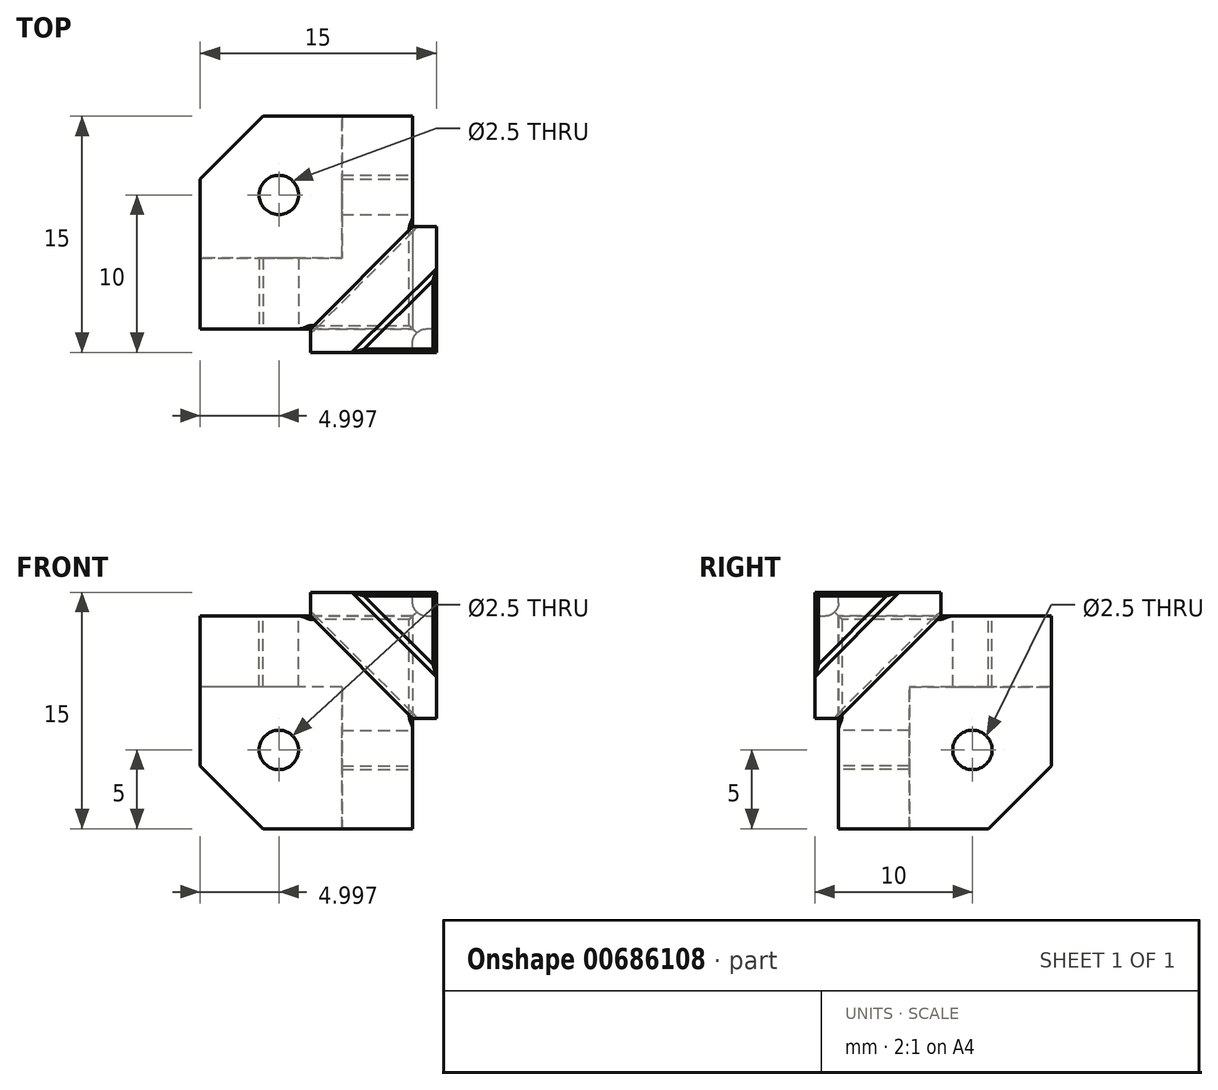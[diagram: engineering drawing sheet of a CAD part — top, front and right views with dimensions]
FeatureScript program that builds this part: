
annotation { "Feature Type Name" : "Feature", "Feature Type Description" : "" }
export const myFeature = defineFeature(function(context is Context, id is Id, definition is map)
    precondition{}
    {
        {
            var Q0;
            Q0=qCreatedBy(makeId("Front.planeOp"),FACE);
            var sketch = newSketch(context, id + "F0", { "sketchPlane" : qUnion([Q0])});
            skLineSegment(sketch, "E0", {"start": v(7.23, 37.22) * mm, "end": v(15.23, 37.22) * mm});
            skLineSegment(sketch, "E1", {"start": v(15.23, 37.22) * mm, "end": v(15.23, 29.22) * mm});
            skLineSegment(sketch, "E2", {"start": v(15.23, 29.22) * mm, "end": v(13.73, 29.22) * mm});
            skLineSegment(sketch, "E3", {"start": v(13.73, 29.22) * mm, "end": v(7.23, 35.72) * mm});
            skLineSegment(sketch, "E4", {"start": v(7.23, 35.72) * mm, "end": v(7.23, 37.22) * mm});
            skLineSegment(sketch, "E5", {"start": v(15.23, 29.22) * mm, "end": v(15.23, 27.22) * mm, "construction": true});
            skLineSegment(sketch, "E6", {"start": v(15.23, 27.22) * mm, "end": v(5.23, 27.22) * mm, "construction": true});
            skCircle(sketch, "E7", {"center": v(5.23, 27.22) * mm, "radius": 1.25 * mm});
            skLineSegment(sketch, "E8", {"start": v(7.23, 37.22) * mm, "end": v(0.23, 37.22) * mm});
            skLineSegment(sketch, "E9", {"start": v(0.23, 37.22) * mm, "end": v(0.23, 26.22) * mm});
            skLineSegment(sketch, "E10", {"start": v(0.23, 26.22) * mm, "end": v(4.23, 22.22) * mm});
            skLineSegment(sketch, "E11", {"start": v(4.23, 22.22) * mm, "end": v(15.23, 22.22) * mm});
            skLineSegment(sketch, "E12", {"start": v(15.23, 22.22) * mm, "end": v(15.23, 29.22) * mm});
            skSolve(sketch);
        }
        {
            var Q0;
            Q0=makeQuery(id+"F0.imprint","IMPRINT",FACE,{"disambiguationData":[TD([[makeQuery(id+"F0.imprint","IMPRINT",EDGE,{"derivedFrom":sQuery(id+"F0.wireOp",EDGE,"E0")}),-1.0]])]});
            extrude(context, id + "F1", {"entities" : qUnion([Q0]), "depth" : 1.5 * mm, "offsetDistance" : 25 * mm});
        }
        {
            var Q0;
            Q0=makeQuery(id+"F0.imprint","IMPRINT",FACE,{"disambiguationData":[TD([[makeQuery(id+"F0.imprint","IMPRINT",EDGE,{"derivedFrom":sQuery(id+"F0.wireOp",EDGE,"E2")}),1.0]])]});
            var Q1;
            Q1=makeQuery(id+"F0.imprint","IMPRINT",FACE,{"disambiguationData":[TD([[makeQuery(id+"F0.imprint","IMPRINT",EDGE,{"derivedFrom":sQuery(id+"F0.wireOp",EDGE,"E0")}),-1.0]])]});
            extrude(context, id + "F2", {"entities" : qUnion([Q0, Q1]), "operationType" : NewBodyOperationType.ADD, "oppositeDirection" : true, "depth" : 3.5 * mm, "offsetDistance" : 25 * mm});
        }
        {
            var Q0;
            {var subQ0=sQuery(id+"F0.wireOp",EDGE,"E0");Q0=makeQuery(id+"F2.boolean.opBoolean","MERGE",FACE,{"derivedFrom":[makeQuery(id+"F1.opExtrude","SWEPT_FACE",FACE,{"disambiguationData":[OSD([subQ0])]}),makeQuery(id+"F2.opExtrude","SWEPT_FACE",FACE,{"disambiguationData":[OSD([subQ0,sQuery(id+"F0.wireOp",EDGE,"E8")])]})]});}
            var sketch = newSketch(context, id + "F3", { "sketchPlane" : qUnion([Q0])});
            skLineSegment(sketch, "E13", {"start": v(7.23, -1.5) * mm, "end": v(15.23, -1.5) * mm});
            skLineSegment(sketch, "E14", {"start": v(15.23, -1.5) * mm, "end": v(15.23, 6.5) * mm});
            skLineSegment(sketch, "E15", {"start": v(15.23, 6.5) * mm, "end": v(13.73, 6.5) * mm});
            skLineSegment(sketch, "E16", {"start": v(13.73, 6.5) * mm, "end": v(7.23, 0) * mm});
            skLineSegment(sketch, "E17", {"start": v(13.73, 6.5) * mm, "end": v(13.73, 13.5) * mm});
            skLineSegment(sketch, "E18", {"start": v(13.73, 13.5) * mm, "end": v(4.23, 13.5) * mm});
            skLineSegment(sketch, "E19", {"start": v(4.23, 13.5) * mm, "end": v(0.23, 9.5) * mm});
            skPoint(sketch, "E19.endSnap0", {"position": v(0.23, 1.75) * mm});
            skLineSegment(sketch, "E20", {"start": v(0.23, 9.5) * mm, "end": v(0.23, 0) * mm});
            skLineSegment(sketch, "E21", {"start": v(8.02, -1.5) * mm, "end": v(5.23, -1.5) * mm, "construction": true});
            skLineSegment(sketch, "E22", {"start": v(5.23, -1.5) * mm, "end": v(5.23, 8.5) * mm, "construction": true});
            skCircle(sketch, "E23", {"center": v(5.23, 8.5) * mm, "radius": 1.25 * mm});
            skSolve(sketch);
        }
        {
            var Q0;
            {var subQ1=sQuery(id+"F3.wireOp",EDGE,"E17");Q0=makeQuery(id+"F3.imprint","IMPRINT",FACE,{"disambiguationData":[TD([[makeQuery(id+"F3.imprint","IMPRINT",EDGE,{"derivedFrom":subQ1}),1.0]])]});}
            var Q1;
            {var subQ3=sQuery(id+"F3.wireOp",EDGE,"E15");Q1=makeQuery(id+"F3.imprint","IMPRINT",FACE,{"disambiguationData":[TD([[makeQuery(id+"F3.imprint","IMPRINT",EDGE,{"derivedFrom":subQ3}),1.0]])]});}
            extrude(context, id + "F4", {"entities" : qUnion([Q0, Q1]), "operationType" : NewBodyOperationType.ADD, "oppositeDirection" : true, "depth" : 5 * mm, "offsetDistance" : 25 * mm});
        }
        {
            var Q0;
            {var subQ1=sQuery(id+"F3.wireOp",EDGE,"E17");Q0=makeQuery(id+"F3.imprint","IMPRINT",FACE,{"disambiguationData":[TD([[makeQuery(id+"F3.imprint","IMPRINT",EDGE,{"derivedFrom":subQ1}),1.0]])]});}
            var Q1;
            {var subQ1=sQuery(id+"F0.wireOp",EDGE,"E8");var subQ2=sQuery(id+"F0.wireOp",EDGE,"E0");var subQ3=makeQuery(id+"F2.opExtrude","CAP_EDGE",EDGE,{"disambiguationData":[OSD([subQ2,subQ1])],"isStart":true});Q1=makeQuery(id+"F3.imprint","IMPRINT",FACE,{"disambiguationData":[TD([[makeQuery(id+"F3.imprint","IMPRINT",EDGE,{"derivedFrom":subQ3}),-1.0]])]});}
            extrude(context, id + "F5", {"entities" : qUnion([Q0, Q1]), "operationType" : NewBodyOperationType.REMOVE, "oppositeDirection" : true, "depth" : 1.5 * mm, "offsetDistance" : 25 * mm});
        }
        {
            var Q0;
            {var subQ0=sQuery(id+"F0.wireOp",EDGE,"E1");Q0=makeQuery(id+"F2.boolean.opBoolean","MERGE",FACE,{"derivedFrom":[makeQuery(id+"F1.opExtrude","SWEPT_FACE",FACE,{"disambiguationData":[OSD([subQ0])]}),makeQuery(id+"F2.opExtrude","SWEPT_FACE",FACE,{"disambiguationData":[OSD([subQ0,sQuery(id+"F0.wireOp",EDGE,"E12")])]})]});}
            var sketch = newSketch(context, id + "F6", { "sketchPlane" : qUnion([Q0])});
            skLineSegment(sketch, "E24", {"start": v(0, 29.22) * mm, "end": v(0, 22.22) * mm});
            skLineSegment(sketch, "E25", {"start": v(0, 22.22) * mm, "end": v(9.5, 22.22) * mm});
            skLineSegment(sketch, "E26", {"start": v(13.5, 35.72) * mm, "end": v(13.5, 26.22) * mm});
            skLineSegment(sketch, "E27", {"start": v(13.5, 26.22) * mm, "end": v(9.5, 22.22) * mm});
            skLineSegment(sketch, "E28", {"start": v(-1.5, 29.22) * mm, "end": v(-1.5, 27.22) * mm, "construction": true});
            skLineSegment(sketch, "E29", {"start": v(-1.5, 27.22) * mm, "end": v(8.5, 27.22) * mm, "construction": true});
            skCircle(sketch, "E30", {"center": v(8.5, 27.22) * mm, "radius": 1.25 * mm});
            skLineSegment(sketch, "E31", {"start": v(13.5, 35.72) * mm, "end": v(6.5, 35.72) * mm});
            skLineSegment(sketch, "E32", {"start": v(6.5, 35.72) * mm, "end": v(0, 29.22) * mm});
            skSolve(sketch);
        }
        {
            var Q0;
            Q0=qSketchRegion(id+"F6",true);
            extrude(context, id + "F7", {"entities" : qUnion([Q0]), "operationType" : NewBodyOperationType.ADD, "oppositeDirection" : true, "depth" : 5 * mm, "offsetDistance" : 25 * mm});
        }
        {
            var Q0;
            {var subQ2=sQuery(id+"F6.wireOp",EDGE,"E24");Q0=makeQuery(id+"F6.imprint","IMPRINT",FACE,{"disambiguationData":[TD([[makeQuery(id+"F6.imprint","IMPRINT",EDGE,{"derivedFrom":subQ2}),-1.0]])]});}
            var Q1;
            Q1=makeQuery(id+"F6.imprint","IMPRINT",FACE,{"disambiguationData":[TD([[makeQuery(id+"F6.imprint","IMPRINT",EDGE,{"derivedFrom":sQuery(id+"F6.wireOp",EDGE,"E26")}),-1.0]])]});
            var Q2;
            {var subQ1=sQuery(id+"F3.wireOp",EDGE,"E14");var subQ2=makeQuery(id+"F4.opExtrude","CAP_EDGE",EDGE,{"disambiguationData":[OSD([subQ1])],"isStart":false});Q2=makeQuery(id+"F6.imprint","IMPRINT",FACE,{"disambiguationData":[TD([[makeQuery(id+"F6.imprint","IMPRINT",EDGE,{"derivedFrom":subQ2}),1.0]])]});}
            extrude(context, id + "F8", {"entities" : qUnion([Q0, Q1, Q2]), "operationType" : NewBodyOperationType.REMOVE, "oppositeDirection" : true, "depth" : 1.5 * mm, "offsetDistance" : 25 * mm});
        }
        {
            var Q0;
            Q0=makeQuery(id+"F1.opExtrude","CAP_FACE",FACE,{"disambiguationData":[OSD([sQuery(id+"F0.wireOp",EDGE,"E0"),sQuery(id+"F0.wireOp",EDGE,"E1"),sQuery(id+"F0.wireOp",EDGE,"E2"),sQuery(id+"F0.wireOp",EDGE,"E3"),sQuery(id+"F0.wireOp",EDGE,"E4")])],"isStart":false});
            var sketch = newSketch(context, id + "F9", { "sketchPlane" : qUnion([Q0])});
            skLineSegment(sketch, "E33", {"start": v(15.23, 37.22) * mm, "end": v(15.23, 32.22) * mm});
            skLineSegment(sketch, "E34", {"start": v(15.23, 32.22) * mm, "end": v(10.23, 37.22) * mm});
            skLineSegment(sketch, "E35", {"start": v(10.23, 37.22) * mm, "end": v(15.23, 37.22) * mm});
            skSolve(sketch);
        }
        {
            var Q0;
            Q0=makeQuery(id+"F9.imprint","IMPRINT",FACE,{"disambiguationData":[TD([[makeQuery(id+"F9.imprint","IMPRINT",EDGE,{"derivedFrom":sQuery(id+"F9.wireOp",EDGE,"E33")}),-1.0]])]});
            extrude(context, id + "F10", {"entities" : qUnion([Q0]), "operationType" : NewBodyOperationType.REMOVE, "oppositeDirection" : true, "depth" : 5 * mm, "offsetDistance" : 25 * mm});
        }
        {
            var Q0;
            Q0=makeQuery(id+"F10.boolean.opBoolean","COPY",EDGE,{"derivedFrom":makeQuery(id+"F10.opExtrude","CAP_EDGE",EDGE,{"disambiguationData":[OSD([sQuery(id+"F9.wireOp",EDGE,"E34")])],"isStart":false})});
            chamfer(context, id + "F11", {"entities" : qUnion([Q0]), "chamferType" : ChamferType.OFFSET_ANGLE, "width" : 5 * mm, "oppositeDirection" : false, "angle" : 35.4 * degree, "tangentPropagation" : true});
        }
        {
            var Q0;
            Q0=makeQuery(id+"F11.opChamfer","BLEND_EDGE",EDGE,{"blendedFrom":[makeQuery(id+"F10.boolean.opBoolean","COPY",EDGE,{"derivedFrom":makeQuery(id+"F10.opExtrude","CAP_EDGE",EDGE,{"disambiguationData":[OSD([sQuery(id+"F9.wireOp",EDGE,"E34")])],"isStart":false})}),makeQuery(id+"F1.opExtrude","CAP_FACE",FACE,{"disambiguationData":[OSD([sQuery(id+"F0.wireOp",EDGE,"E0"),sQuery(id+"F0.wireOp",EDGE,"E1"),sQuery(id+"F0.wireOp",EDGE,"E2"),sQuery(id+"F0.wireOp",EDGE,"E3"),sQuery(id+"F0.wireOp",EDGE,"E4")])],"isStart":false})],"blendedInto":[makeQuery(id+"F1.opExtrude","CAP_FACE",FACE,{"disambiguationData":[OSD([sQuery(id+"F0.wireOp",EDGE,"E0"),sQuery(id+"F0.wireOp",EDGE,"E1"),sQuery(id+"F0.wireOp",EDGE,"E2"),sQuery(id+"F0.wireOp",EDGE,"E3"),sQuery(id+"F0.wireOp",EDGE,"E4")])],"isStart":false})]});
            var Q1;
            {var subQ0=sQuery(id+"F0.wireOp",EDGE,"E8");var subQ1=sQuery(id+"F0.wireOp",EDGE,"E0");Q1=makeQuery(id+"F11.opChamfer","BLEND_EDGE",EDGE,{"blendedFrom":[makeQuery(id+"F10.boolean.opBoolean","COPY",EDGE,{"derivedFrom":makeQuery(id+"F10.opExtrude","CAP_EDGE",EDGE,{"disambiguationData":[OSD([sQuery(id+"F9.wireOp",EDGE,"E34")])],"isStart":false})}),makeQuery(id+"F4.boolean.opBoolean","MERGE",FACE,{"derivedFrom":[makeQuery(id+"F2.boolean.opBoolean","MERGE",FACE,{"derivedFrom":[makeQuery(id+"F1.opExtrude","SWEPT_FACE",FACE,{"disambiguationData":[OSD([subQ1])]}),makeQuery(id+"F2.opExtrude","SWEPT_FACE",FACE,{"disambiguationData":[OSD([subQ1,subQ0])]})]}),makeQuery(id+"F4.opExtrude","CAP_FACE",FACE,{"disambiguationData":[OSD([subQ1,subQ0,sQuery(id+"F3.wireOp",EDGE,"id0TNCpU-tjdV-AgSU-QIlH-1rNdUmwGPP8J"),sQuery(id+"F3.wireOp",EDGE,"mGFVvrbr-tIrU-syV4-yza1-VgwdehKtnJvE"),sQuery(id+"F3.wireOp",EDGE,"wSTTxPhp-j6Tf-tGPT-JtDE-c5HYP9l80gTy"),sQuery(id+"F3.wireOp",EDGE,"6f74HBZF-W9bh-Bztp-LMnC-ap8Q1K5RPxhI"),sQuery(id+"F3.wireOp",EDGE,"pXlPqK1o-hzZR-9fDG-u2KL-nj3FlQz3lFwb")])],"isStart":true})]})],"blendedInto":[makeQuery(id+"F4.boolean.opBoolean","MERGE",FACE,{"derivedFrom":[makeQuery(id+"F2.boolean.opBoolean","MERGE",FACE,{"derivedFrom":[makeQuery(id+"F1.opExtrude","SWEPT_FACE",FACE,{"disambiguationData":[OSD([subQ1])]}),makeQuery(id+"F2.opExtrude","SWEPT_FACE",FACE,{"disambiguationData":[OSD([subQ1,subQ0])]})]}),makeQuery(id+"F4.opExtrude","CAP_FACE",FACE,{"disambiguationData":[OSD([subQ1,subQ0,sQuery(id+"F3.wireOp",EDGE,"id0TNCpU-tjdV-AgSU-QIlH-1rNdUmwGPP8J"),sQuery(id+"F3.wireOp",EDGE,"mGFVvrbr-tIrU-syV4-yza1-VgwdehKtnJvE"),sQuery(id+"F3.wireOp",EDGE,"wSTTxPhp-j6Tf-tGPT-JtDE-c5HYP9l80gTy"),sQuery(id+"F3.wireOp",EDGE,"6f74HBZF-W9bh-Bztp-LMnC-ap8Q1K5RPxhI"),sQuery(id+"F3.wireOp",EDGE,"pXlPqK1o-hzZR-9fDG-u2KL-nj3FlQz3lFwb")])],"isStart":true})]})]});}
            var Q2;
            {var subQ0=sQuery(id+"F0.wireOp",EDGE,"E1");Q2=makeQuery(id+"F11.opChamfer","BLEND_EDGE",EDGE,{"blendedFrom":[makeQuery(id+"F10.boolean.opBoolean","COPY",EDGE,{"derivedFrom":makeQuery(id+"F10.opExtrude","CAP_EDGE",EDGE,{"disambiguationData":[OSD([sQuery(id+"F9.wireOp",EDGE,"E34")])],"isStart":false})}),makeQuery(id+"F7.boolean.opBoolean","MERGE",FACE,{"derivedFrom":[makeQuery(id+"F2.boolean.opBoolean","MERGE",FACE,{"derivedFrom":[makeQuery(id+"F1.opExtrude","SWEPT_FACE",FACE,{"disambiguationData":[OSD([subQ0])]}),makeQuery(id+"F2.opExtrude","SWEPT_FACE",FACE,{"disambiguationData":[OSD([subQ0,sQuery(id+"F0.wireOp",EDGE,"E12")])]})]}),makeQuery(id+"F7.opExtrude","CAP_FACE",FACE,{"disambiguationData":[OSD([sQuery(id+"F6.wireOp",EDGE,"bjqw6rF1-9aoZ-1MRt-8oHp-ZjFiTM0oOFLL"),sQuery(id+"F6.wireOp",EDGE,"E24"),sQuery(id+"F6.wireOp",EDGE,"E25"),sQuery(id+"F6.wireOp",EDGE,"4vnc1qx3-YKp5-J8BV-yxKJ-AHBmvpOXDA1h"),sQuery(id+"F6.wireOp",EDGE,"E26"),sQuery(id+"F6.wireOp",EDGE,"E27"),sQuery(id+"F6.wireOp",EDGE,"E30")])],"isStart":true})]})],"blendedInto":[makeQuery(id+"F7.boolean.opBoolean","MERGE",FACE,{"derivedFrom":[makeQuery(id+"F2.boolean.opBoolean","MERGE",FACE,{"derivedFrom":[makeQuery(id+"F1.opExtrude","SWEPT_FACE",FACE,{"disambiguationData":[OSD([subQ0])]}),makeQuery(id+"F2.opExtrude","SWEPT_FACE",FACE,{"disambiguationData":[OSD([subQ0,sQuery(id+"F0.wireOp",EDGE,"E12")])]})]}),makeQuery(id+"F7.opExtrude","CAP_FACE",FACE,{"disambiguationData":[OSD([sQuery(id+"F6.wireOp",EDGE,"bjqw6rF1-9aoZ-1MRt-8oHp-ZjFiTM0oOFLL"),sQuery(id+"F6.wireOp",EDGE,"E24"),sQuery(id+"F6.wireOp",EDGE,"E25"),sQuery(id+"F6.wireOp",EDGE,"4vnc1qx3-YKp5-J8BV-yxKJ-AHBmvpOXDA1h"),sQuery(id+"F6.wireOp",EDGE,"E26"),sQuery(id+"F6.wireOp",EDGE,"E27"),sQuery(id+"F6.wireOp",EDGE,"E30")])],"isStart":true})]})]});}
            chamfer(context, id + "F12", {"entities" : qUnion([Q0, Q1, Q2]), "width" : .5 * mm, "tangentPropagation" : true});
        }
        {
            var Q0;
            {var subQ0=sQuery(id+"F0.wireOp",EDGE,"E2");Q0=makeQuery(id+"F8.boolean.opBoolean","MERGE",VERTEX,{"derivedFrom":[makeQuery(id+"F1.opExtrude","CAP_VERTEX",VERTEX,{"disambiguationData":[OSD([subQ0,sQuery(id+"F0.wireOp",EDGE,"E3")])],"isStart":true}),makeQuery(id+"F8.opExtrude","CAP_VERTEX",VERTEX,{"disambiguationData":[OSD([sQuery(id+"F0.wireOp",EDGE,"E1"),subQ0,sQuery(id+"F0.wireOp",EDGE,"E12"),sQuery(id+"F6.wireOp",EDGE,"E24"),sQuery(id+"F6.wireOp",EDGE,"E32")])],"isStart":false})]});}
            var Q1;
            {var subQ0=sQuery(id+"F0.wireOp",EDGE,"E4");Q1=makeQuery(id+"F5.boolean.opBoolean","MERGE",VERTEX,{"derivedFrom":[makeQuery(id+"F1.opExtrude","CAP_VERTEX",VERTEX,{"disambiguationData":[OSD([sQuery(id+"F0.wireOp",EDGE,"E3"),subQ0])],"isStart":true}),makeQuery(id+"F5.opExtrude","CAP_VERTEX",VERTEX,{"disambiguationData":[OSD([sQuery(id+"F0.wireOp",EDGE,"E0"),subQ0,sQuery(id+"F0.wireOp",EDGE,"E8"),sQuery(id+"F3.wireOp",EDGE,"E16")])],"isStart":false})]});}
            var Q2;
            {var subQ0=sQuery(id+"F3.wireOp",EDGE,"E15");Q2=makeQuery(id+"F8.boolean.opBoolean","MERGE",VERTEX,{"derivedFrom":[makeQuery(id+"F5.boolean.opBoolean","COPY",VERTEX,{"derivedFrom":makeQuery(id+"F5.opExtrude","CAP_VERTEX",VERTEX,{"disambiguationData":[OSD([subQ0,sQuery(id+"F3.wireOp",EDGE,"E16"),sQuery(id+"F3.wireOp",EDGE,"E17")])],"isStart":false})}),makeQuery(id+"F8.opExtrude","CAP_VERTEX",VERTEX,{"disambiguationData":[OSD([sQuery(id+"F3.wireOp",EDGE,"E14"),subQ0,sQuery(id+"F6.wireOp",EDGE,"E31"),sQuery(id+"F6.wireOp",EDGE,"E32")])],"isStart":false})]});}
            cPlane(context, id + "F13", {"entities" : qUnion([Q0, Q1, Q2]), "cplaneType" : CPlaneType.THREE_POINT, "offset" : 25 * mm, "width" : 150 * mm, "height" : 150 * mm});
        }
        {
            var Q0;
            Q0=qCreatedBy(id+"F13.planeOp",FACE);
            var sketch = newSketch(context, id + "F14", { "sketchPlane" : qUnion([Q0])});
            skLineSegment(sketch, "E36", {"start": v(-8.68, 25.26) * mm, "end": v(-0.72, 20.66) * mm});
            skLineSegment(sketch, "E37", {"start": v(-0.72, 29.85) * mm, "end": v(-8.68, 25.26) * mm});
            skLineSegment(sketch, "E38", {"start": v(-0.72, 20.66) * mm, "end": v(-0.72, 29.85) * mm});
            skLineSegment(sketch, "E39.0", {"start": v(-0.92, 29.5) * mm, "end": v(-8.28, 25.26) * mm});
            skLineSegment(sketch, "E39.1", {"start": v(-0.92, 21) * mm, "end": v(-0.92, 29.5) * mm});
            skLineSegment(sketch, "E39.2", {"start": v(-8.28, 25.26) * mm, "end": v(-0.92, 21) * mm});
            skLineSegment(sketch, "E40.0", {"start": v(0.16, 31.38) * mm, "end": v(-10.44, 25.26) * mm});
            skLineSegment(sketch, "E40.1", {"start": v(0.16, 19.14) * mm, "end": v(0.16, 31.38) * mm});
            skLineSegment(sketch, "E40.2", {"start": v(-10.44, 25.26) * mm, "end": v(0.16, 19.14) * mm});
            skSolve(sketch);
        }
        {
            var Q0;
            Q0=qSketchRegion(id+"F14",true);
            var Q1;
            Q1=makeQuery(id+"F14.imprint","IMPRINT",FACE,{"disambiguationData":[TD([[makeQuery(id+"F14.imprint","IMPRINT",EDGE,{"derivedFrom":sQuery(id+"F14.wireOp",EDGE,"E36")}),1.0]])]});
            extrude(context, id + "F15", {"entities" : qUnion([Q0, Q1]), "operationType" : NewBodyOperationType.REMOVE, "endBound" : BoundingType.SYMMETRIC, "depth" : .6 * mm, "offsetDistance" : 25 * mm});
        }
        {
            var Q0;
            Q0=makeQuery(id+"F15.boolean.opBoolean","COPY",EDGE,{"derivedFrom":makeQuery(id+"F15.opExtrude","CAP_EDGE",EDGE,{"disambiguationData":[OSD([sQuery(id+"F14.wireOp",EDGE,"E39.0")])],"isStart":true})});
            var Q1;
            Q1=makeQuery(id+"F15.boolean.opBoolean","COPY",EDGE,{"derivedFrom":makeQuery(id+"F15.opExtrude","CAP_EDGE",EDGE,{"disambiguationData":[OSD([sQuery(id+"F14.wireOp",EDGE,"E39.1")])],"isStart":true})});
            var Q2;
            Q2=makeQuery(id+"F15.boolean.opBoolean","COPY",EDGE,{"derivedFrom":makeQuery(id+"F15.opExtrude","CAP_EDGE",EDGE,{"disambiguationData":[OSD([sQuery(id+"F14.wireOp",EDGE,"E39.0")])],"isStart":false})});
            var Q3;
            Q3=makeQuery(id+"F15.boolean.opBoolean","COPY",EDGE,{"derivedFrom":makeQuery(id+"F15.opExtrude","CAP_EDGE",EDGE,{"disambiguationData":[OSD([sQuery(id+"F14.wireOp",EDGE,"E39.1")])],"isStart":false})});
            var Q4;
            Q4=makeQuery(id+"F15.boolean.opBoolean","COPY",EDGE,{"derivedFrom":makeQuery(id+"F15.opExtrude","CAP_EDGE",EDGE,{"disambiguationData":[OSD([sQuery(id+"F14.wireOp",EDGE,"E39.2")])],"isStart":true})});
            var Q5;
            Q5=makeQuery(id+"F15.boolean.opBoolean","COPY",EDGE,{"derivedFrom":makeQuery(id+"F15.opExtrude","CAP_EDGE",EDGE,{"disambiguationData":[OSD([sQuery(id+"F14.wireOp",EDGE,"E39.2")])],"isStart":false})});
            fillet(context, id + "F16", {"entities" : qUnion([Q0, Q1, Q2, Q3, Q4, Q5]), "radius" : .3 * mm, "tangentPropagation" : true, "allowEdgeOverflow" : false});
        }
        {
            var Q0;
            Q0=makeQuery(id+"F15.boolean.opBoolean","INTERSECT",EDGE,{"derivedFrom":[makeQuery(id+"F8.boolean.opBoolean","COPY",FACE,{"derivedFrom":makeQuery(id+"F8.opExtrude","SWEPT_FACE",FACE,{"disambiguationData":[OSD([sQuery(id+"F6.wireOp",EDGE,"E32")])]})}),makeQuery(id+"F15.opExtrude","CAP_FACE",FACE,{"disambiguationData":[OSD([sQuery(id+"F14.wireOp",EDGE,"E39.0"),sQuery(id+"F14.wireOp",EDGE,"E39.1"),sQuery(id+"F14.wireOp",EDGE,"E39.2"),sQuery(id+"F14.wireOp",EDGE,"E40.0"),sQuery(id+"F14.wireOp",EDGE,"E40.1"),sQuery(id+"F14.wireOp",EDGE,"E40.2")])],"isStart":false})]});
            var Q1;
            Q1=makeQuery(id+"F15.boolean.opBoolean","INTERSECT",EDGE,{"derivedFrom":[makeQuery(id+"F1.opExtrude","SWEPT_FACE",FACE,{"disambiguationData":[OSD([sQuery(id+"F0.wireOp",EDGE,"E3")])]}),makeQuery(id+"F15.opExtrude","CAP_FACE",FACE,{"disambiguationData":[OSD([sQuery(id+"F14.wireOp",EDGE,"E39.0"),sQuery(id+"F14.wireOp",EDGE,"E39.1"),sQuery(id+"F14.wireOp",EDGE,"E39.2"),sQuery(id+"F14.wireOp",EDGE,"E40.0"),sQuery(id+"F14.wireOp",EDGE,"E40.1"),sQuery(id+"F14.wireOp",EDGE,"E40.2")])],"isStart":false})]});
            var Q2;
            Q2=makeQuery(id+"F15.boolean.opBoolean","INTERSECT",EDGE,{"derivedFrom":[makeQuery(id+"F5.boolean.opBoolean","COPY",FACE,{"derivedFrom":makeQuery(id+"F5.opExtrude","SWEPT_FACE",FACE,{"disambiguationData":[OSD([sQuery(id+"F3.wireOp",EDGE,"E16")])]})}),makeQuery(id+"F15.opExtrude","CAP_FACE",FACE,{"disambiguationData":[OSD([sQuery(id+"F14.wireOp",EDGE,"E39.0"),sQuery(id+"F14.wireOp",EDGE,"E39.1"),sQuery(id+"F14.wireOp",EDGE,"E39.2"),sQuery(id+"F14.wireOp",EDGE,"E40.0"),sQuery(id+"F14.wireOp",EDGE,"E40.1"),sQuery(id+"F14.wireOp",EDGE,"E40.2")])],"isStart":false})]});
            fillet(context, id + "F17", {"entities" : qUnion([Q0, Q1, Q2]), "radius" : 1 * mm, "tangentPropagation" : true, "allowEdgeOverflow" : false});
        }
        {
            var Q0;
            Q0=makeQuery(id+"F15.boolean.opBoolean","INTERSECT",EDGE,{"derivedFrom":[makeQuery(id+"F2.opExtrude","CAP_FACE",FACE,{"disambiguationData":[OSD([sQuery(id+"F0.wireOp",EDGE,"E0"),sQuery(id+"F0.wireOp",EDGE,"E1"),sQuery(id+"F0.wireOp",EDGE,"E7"),sQuery(id+"F0.wireOp",EDGE,"E8"),sQuery(id+"F0.wireOp",EDGE,"E9"),sQuery(id+"F0.wireOp",EDGE,"E10"),sQuery(id+"F0.wireOp",EDGE,"E11"),sQuery(id+"F0.wireOp",EDGE,"E12")])],"isStart":true}),makeQuery(id+"F15.opExtrude","CAP_FACE",FACE,{"disambiguationData":[OSD([sQuery(id+"F14.wireOp",EDGE,"E39.0"),sQuery(id+"F14.wireOp",EDGE,"E39.1"),sQuery(id+"F14.wireOp",EDGE,"E39.2"),sQuery(id+"F14.wireOp",EDGE,"E40.0"),sQuery(id+"F14.wireOp",EDGE,"E40.1"),sQuery(id+"F14.wireOp",EDGE,"E40.2")])],"isStart":true})]});
            var Q1;
            Q1=makeQuery(id+"F15.boolean.opBoolean","INTERSECT",EDGE,{"derivedFrom":[makeQuery(id+"F8.boolean.opBoolean","COPY",FACE,{"derivedFrom":makeQuery(id+"F8.opExtrude","CAP_FACE",FACE,{"disambiguationData":[OSD([sQuery(id+"F6.wireOp",EDGE,"E24"),sQuery(id+"F6.wireOp",EDGE,"E25"),sQuery(id+"F6.wireOp",EDGE,"E26"),sQuery(id+"F6.wireOp",EDGE,"E27"),sQuery(id+"F6.wireOp",EDGE,"E30"),sQuery(id+"F6.wireOp",EDGE,"E31"),sQuery(id+"F6.wireOp",EDGE,"E32")])],"isStart":false})}),makeQuery(id+"F15.opExtrude","CAP_FACE",FACE,{"disambiguationData":[OSD([sQuery(id+"F14.wireOp",EDGE,"E39.0"),sQuery(id+"F14.wireOp",EDGE,"E39.1"),sQuery(id+"F14.wireOp",EDGE,"E39.2"),sQuery(id+"F14.wireOp",EDGE,"E40.0"),sQuery(id+"F14.wireOp",EDGE,"E40.1"),sQuery(id+"F14.wireOp",EDGE,"E40.2")])],"isStart":true})]});
            var Q2;
            Q2=makeQuery(id+"F15.boolean.opBoolean","INTERSECT",EDGE,{"derivedFrom":[makeQuery(id+"F7.boolean.opBoolean","MERGE",FACE,{"derivedFrom":[makeQuery(id+"F5.boolean.opBoolean","COPY",FACE,{"derivedFrom":makeQuery(id+"F5.opExtrude","CAP_FACE",FACE,{"disambiguationData":[OSD([sQuery(id+"F0.wireOp",EDGE,"E0"),sQuery(id+"F0.wireOp",EDGE,"E8"),sQuery(id+"F3.wireOp",EDGE,"E16"),sQuery(id+"F3.wireOp",EDGE,"E17"),sQuery(id+"F3.wireOp",EDGE,"E18"),sQuery(id+"F3.wireOp",EDGE,"E19"),sQuery(id+"F3.wireOp",EDGE,"E20"),sQuery(id+"F3.wireOp",EDGE,"E23")])],"isStart":false})}),makeQuery(id+"F7.opExtrude","SWEPT_FACE",FACE,{"disambiguationData":[OSD([sQuery(id+"F6.wireOp",EDGE,"E31")])]})]}),makeQuery(id+"F15.opExtrude","CAP_FACE",FACE,{"disambiguationData":[OSD([sQuery(id+"F14.wireOp",EDGE,"E39.0"),sQuery(id+"F14.wireOp",EDGE,"E39.1"),sQuery(id+"F14.wireOp",EDGE,"E39.2"),sQuery(id+"F14.wireOp",EDGE,"E40.0"),sQuery(id+"F14.wireOp",EDGE,"E40.1"),sQuery(id+"F14.wireOp",EDGE,"E40.2")])],"isStart":true})]});
            fillet(context, id + "F18", {"entities" : qUnion([Q0, Q1, Q2]), "radius" : .2 * mm, "tangentPropagation" : true, "allowEdgeOverflow" : false});
        }
        {
            var Q0;
            Q0=makeQuery(id+"F2.opExtrude","CAP_FACE",FACE,{"disambiguationData":[OSD([sQuery(id+"F0.wireOp",EDGE,"E0"),sQuery(id+"F0.wireOp",EDGE,"E1"),sQuery(id+"F0.wireOp",EDGE,"E7"),sQuery(id+"F0.wireOp",EDGE,"E8"),sQuery(id+"F0.wireOp",EDGE,"E9"),sQuery(id+"F0.wireOp",EDGE,"E10"),sQuery(id+"F0.wireOp",EDGE,"E11"),sQuery(id+"F0.wireOp",EDGE,"E12")])],"isStart":false});
            extrude(context, id + "F19", {"entities" : qUnion([Q0]), "operationType" : NewBodyOperationType.ADD, "depth" : 1 * mm, "offsetDistance" : 25 * mm});
        }
        {
            var Q0;
            Q0=makeQuery(id+"F7.opExtrude","CAP_FACE",FACE,{"disambiguationData":[OSD([sQuery(id+"F6.wireOp",EDGE,"E24"),sQuery(id+"F6.wireOp",EDGE,"E25"),sQuery(id+"F6.wireOp",EDGE,"E26"),sQuery(id+"F6.wireOp",EDGE,"E27"),sQuery(id+"F6.wireOp",EDGE,"E30"),sQuery(id+"F6.wireOp",EDGE,"E31"),sQuery(id+"F6.wireOp",EDGE,"E32")])],"isStart":false});
            extrude(context, id + "F20", {"entities" : qUnion([Q0]), "operationType" : NewBodyOperationType.ADD, "depth" : 1 * mm, "offsetDistance" : 25 * mm});
        }
        {
            var Q0;
            Q0=makeQuery(id+"F4.opExtrude","CAP_FACE",FACE,{"disambiguationData":[OSD([sQuery(id+"F0.wireOp",EDGE,"E0"),sQuery(id+"F0.wireOp",EDGE,"E8"),sQuery(id+"F3.wireOp",EDGE,"E14"),sQuery(id+"F3.wireOp",EDGE,"E15"),sQuery(id+"F3.wireOp",EDGE,"E17"),sQuery(id+"F3.wireOp",EDGE,"E18"),sQuery(id+"F3.wireOp",EDGE,"E19"),sQuery(id+"F3.wireOp",EDGE,"E20"),sQuery(id+"F3.wireOp",EDGE,"E23")])],"isStart":false});
            extrude(context, id + "F21", {"entities" : qUnion([Q0]), "operationType" : NewBodyOperationType.ADD, "depth" : 1 * mm, "offsetDistance" : 25 * mm});
        }
    });
